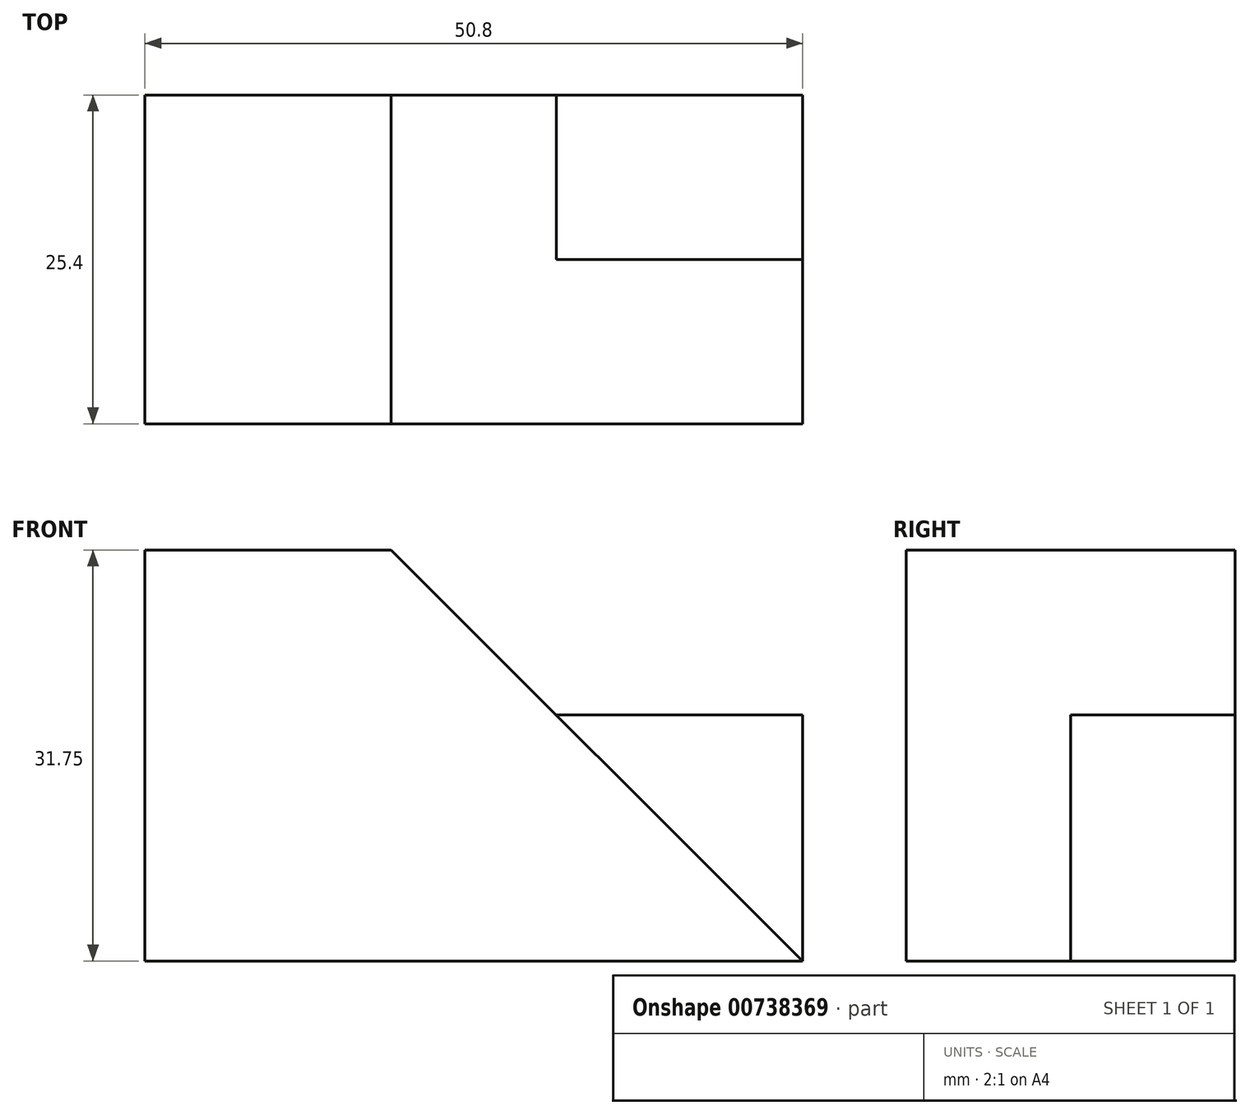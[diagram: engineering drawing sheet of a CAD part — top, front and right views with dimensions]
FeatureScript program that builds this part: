
annotation { "Feature Type Name" : "Feature", "Feature Type Description" : "" }
export const myFeature = defineFeature(function(context is Context, id is Id, definition is map)
    precondition{}
    {
        {
            var Q0;
            Q0=qCreatedBy(makeId("Front.planeOp"),FACE);
            var sketch = newSketch(context, id + "F0", { "sketchPlane" : qUnion([Q0])});
            skLineSegment(sketch, "E0", {"start": v(0, 0) * mm, "end": v(0, 31.75) * mm});
            skLineSegment(sketch, "E1", {"start": v(0, 31.75) * mm, "end": v(50.8, 31.75) * mm});
            skLineSegment(sketch, "E2", {"start": v(50.8, 31.75) * mm, "end": v(50.8, 0) * mm});
            skLineSegment(sketch, "E3", {"start": v(50.8, 0) * mm, "end": v(0, 0) * mm});
            skSolve(sketch);
        }
        {
            var Q0;
            Q0=makeQuery(id+"F0.imprint","IMPRINT",FACE,{"disambiguationData":[TD([[makeQuery(id+"F0.imprint","IMPRINT",EDGE,{"derivedFrom":sQuery(id+"F0.wireOp",EDGE,"E0")}),-1.0]])]});
            extrude(context, id + "F1", {"entities" : qUnion([Q0]), "depth" : 25.4 * mm, "offsetDistance" : 25.4 * mm});
        }
        {
            var Q0;
            Q0=qCreatedBy(makeId("Front.planeOp"),FACE);
            var sketch = newSketch(context, id + "F2", { "sketchPlane" : qUnion([Q0])});
            skLineSegment(sketch, "E4", {"start": v(38.65, -0.44) * mm, "end": v(31.43, 5.73) * mm});
            skLineSegment(sketch, "E5", {"start": v(31.43, 5.73) * mm, "end": v(50.36, 5.73) * mm});
            skLineSegment(sketch, "E6", {"start": v(50.36, 5.73) * mm, "end": v(50.36, 0) * mm});
            skLineSegment(sketch, "E7", {"start": v(50.36, 0) * mm, "end": v(38.65, -0.44) * mm});
            skSolve(sketch);
        }
        {
            var Q0;
            Q0 = qSketchRegion(id + "F2", true);
            extrude(context, id + "F3", {"entities" : qUnion([Q0]), "operationType" : NewBodyOperationType.REMOVE, "oppositeDirection" : true, "depth" : 12.7 * mm, "offsetDistance" : 25.4 * mm});
        }
        {
            var Q0;
            Q0=makeQuery(id+"F1.opExtrude","CAP_FACE",FACE,{"disambiguationData":[OSD([sQuery(id+"F0.wireOp",EDGE,"E0"),sQuery(id+"F0.wireOp",EDGE,"E1"),sQuery(id+"F0.wireOp",EDGE,"E2"),sQuery(id+"F0.wireOp",EDGE,"E3")])],"isStart":false});
            var sketch = newSketch(context, id + "F4", { "sketchPlane" : qUnion([Q0])});
            skLineSegment(sketch, "E8", {"start": v(0, 31.75) * mm, "end": v(19, 31.75) * mm});
            skLineSegment(sketch, "E9", {"start": v(19, 31.75) * mm, "end": v(50.8, 0) * mm});
            skSolve(sketch);
        }
        {
            var Q0;
            {var subQ0=sQuery(id+"F4.wireOp",EDGE,"E9");Q0=makeQuery(id+"F4.imprint","IMPRINT",FACE,{"disambiguationData":[TD([[makeQuery(id+"F4.imprint","IMPRINT",EDGE,{"derivedFrom":subQ0}),1.0]])]});}
            extrude(context, id + "F5", {"entities" : qUnion([Q0]), "operationType" : NewBodyOperationType.REMOVE, "oppositeDirection" : true, "depth" : 12.7 * mm, "offsetDistance" : 25.4 * mm});
        }
        {
            var Q0;
            Q0=makeQuery(id+"F5.boolean.opBoolean","COPY",FACE,{"derivedFrom":makeQuery(id+"F5.opExtrude","CAP_FACE",FACE,{"disambiguationData":[OSD([sQuery(id+"F0.wireOp",EDGE,"E1"),sQuery(id+"F0.wireOp",EDGE,"E2"),sQuery(id+"F4.wireOp",EDGE,"E9")])],"isStart":false})});
            var sketch = newSketch(context, id + "F6", { "sketchPlane" : qUnion([Q0])});
            skLineSegment(sketch, "E10", {"start": v(50.8, 0) * mm, "end": v(50.8, 19) * mm});
            skLineSegment(sketch, "E11", {"start": v(50.8, 19) * mm, "end": v(31.77, 19) * mm});
            skSolve(sketch);
        }
        {
            var Q0;
            {var subQ0=sQuery(id+"F6.wireOp",EDGE,"E11");Q0=makeQuery(id+"F6.imprint","IMPRINT",FACE,{"disambiguationData":[TD([[makeQuery(id+"F6.imprint","IMPRINT",EDGE,{"derivedFrom":subQ0}),-1.0]])]});}
            extrude(context, id + "F7", {"entities" : qUnion([Q0]), "operationType" : NewBodyOperationType.REMOVE, "endBound" : BoundingType.THROUGH_ALL, "oppositeDirection" : true, "depth" : 25.4 * mm, "offsetDistance" : 25.4 * mm});
        }
    });
